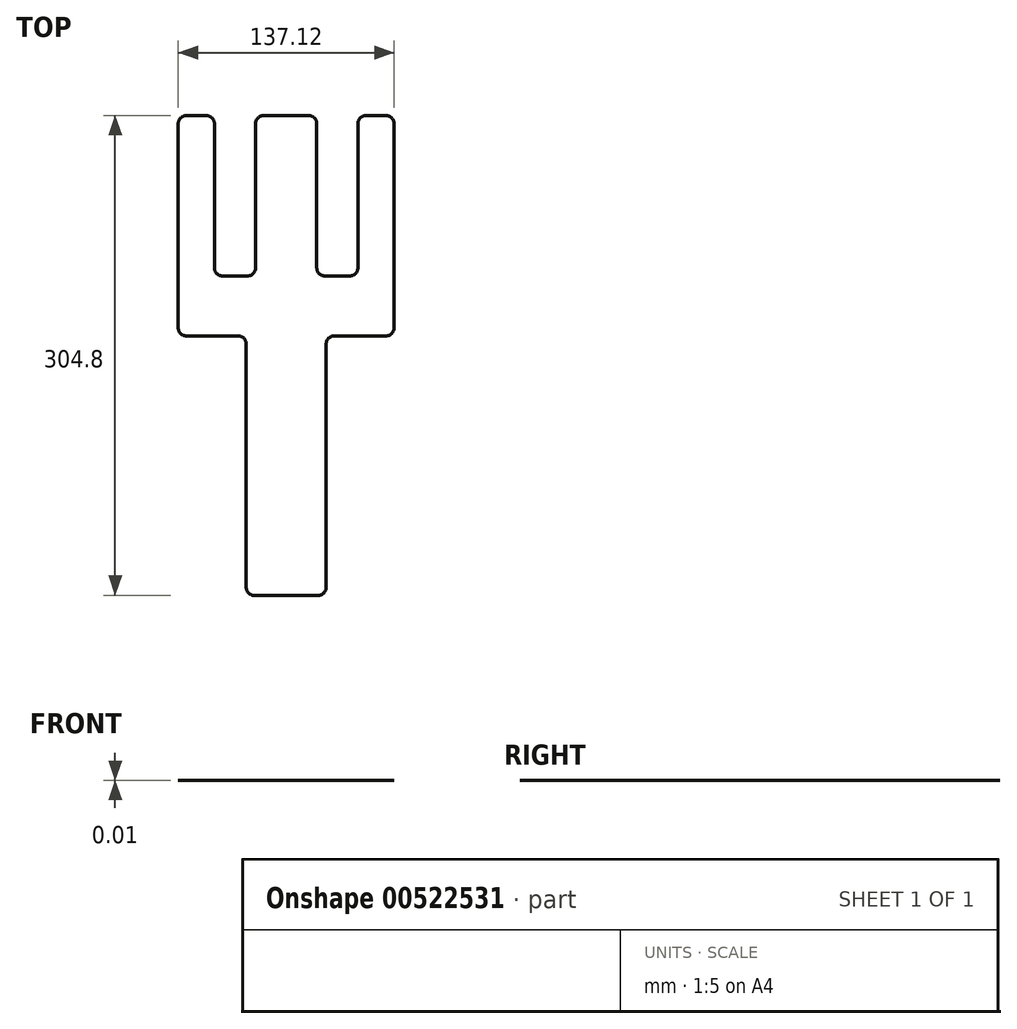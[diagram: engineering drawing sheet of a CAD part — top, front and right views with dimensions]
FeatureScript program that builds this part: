
annotation { "Feature Type Name" : "Feature", "Feature Type Description" : "" }
export const myFeature = defineFeature(function(context is Context, id is Id, definition is map)
    precondition{}
    {
        {
            var Q0;
            Q0=qCreatedBy(makeId("Top.planeOp"),FACE);
            var sketch = newSketch(context, id + "F0", { "sketchPlane" : qUnion([Q0])});
            skLineSegment(sketch, "E0", {"start": v(0, 304.8) * mm, "end": v(-19.44, 304.8) * mm});
            skLineSegment(sketch, "E1", {"start": v(-19.44, 304.8) * mm, "end": v(-19.44, 202.9) * mm});
            skLineSegment(sketch, "E2", {"start": v(-19.44, 202.9) * mm, "end": v(-45.56, 202.9) * mm});
            skLineSegment(sketch, "E3", {"start": v(-45.56, 202.9) * mm, "end": v(-45.56, 304.8) * mm});
            skLineSegment(sketch, "E4", {"start": v(-45.56, 304.8) * mm, "end": v(-68.56, 304.8) * mm});
            skLineSegment(sketch, "E5", {"start": v(-68.56, 304.8) * mm, "end": v(-68.56, 164.8) * mm});
            skLineSegment(sketch, "E6", {"start": v(-68.56, 164.8) * mm, "end": v(-25.4, 164.8) * mm});
            skLineSegment(sketch, "E7", {"start": v(-25.4, 164.8) * mm, "end": v(-25.4, 0) * mm});
            skLineSegment(sketch, "E8", {"start": v(-25.4, 0) * mm, "end": v(0, 0) * mm});
            skLineSegment(sketch, "E9.MirrorCS", {"start": v(25.4, 0) * mm, "end": v(0, 0) * mm});
            skLineSegment(sketch, "E10.MirrorCS", {"start": v(68.56, 164.8) * mm, "end": v(25.4, 164.8) * mm});
            skLineSegment(sketch, "E11.MirrorCS", {"start": v(25.4, 164.8) * mm, "end": v(25.4, 0) * mm});
            skLineSegment(sketch, "E12.MirrorCS", {"start": v(68.56, 304.8) * mm, "end": v(68.56, 164.8) * mm});
            skLineSegment(sketch, "E13.MirrorCS", {"start": v(45.56, 304.8) * mm, "end": v(68.56, 304.8) * mm});
            skLineSegment(sketch, "E14.MirrorCS", {"start": v(45.56, 202.9) * mm, "end": v(45.56, 304.8) * mm});
            skLineSegment(sketch, "E15.MirrorCS", {"start": v(19.44, 202.9) * mm, "end": v(45.56, 202.9) * mm});
            skLineSegment(sketch, "E16.MirrorCS", {"start": v(19.44, 304.8) * mm, "end": v(19.44, 202.9) * mm});
            skLineSegment(sketch, "E17.MirrorCS", {"start": v(0, 304.8) * mm, "end": v(19.44, 304.8) * mm});
            skLineSegment(sketch, "E18", {"start": v(0, 0) * mm, "end": v(0, 304.8) * mm, "construction": true});
            skSolve(sketch);
        }
        {
            var Q0;
            Q0=makeQuery(id+"F0.imprint","IMPRINT",FACE,{"disambiguationData":[TD([[makeQuery(id+"F0.imprint","IMPRINT",EDGE,{"derivedFrom":sQuery(id+"F0.wireOp",EDGE,"E0")}),1.0]])]});
            extrude(context, id + "F1", {"entities" : qUnion([Q0]), "depth" : 3 / 203.2 * mm, "offsetDistance" : 25.4 * mm});
        }
        {
            var Q0;
            Q0=makeQuery(id+"F1.opExtrude","SWEPT_EDGE",EDGE,{"disambiguationData":[OSD([sQuery(id+"F0.wireOp",EDGE,"E12.MirrorCS"),sQuery(id+"F0.wireOp",EDGE,"E13.MirrorCS")])]});
            var Q1;
            Q1=makeQuery(id+"F1.opExtrude","SWEPT_EDGE",EDGE,{"disambiguationData":[OSD([sQuery(id+"F0.wireOp",EDGE,"E13.MirrorCS"),sQuery(id+"F0.wireOp",EDGE,"E14.MirrorCS")])]});
            var Q2;
            Q2=makeQuery(id+"F1.opExtrude","SWEPT_EDGE",EDGE,{"disambiguationData":[OSD([sQuery(id+"F0.wireOp",EDGE,"E16.MirrorCS"),sQuery(id+"F0.wireOp",EDGE,"E17.MirrorCS")])]});
            var Q3;
            Q3=makeQuery(id+"F1.opExtrude","SWEPT_EDGE",EDGE,{"disambiguationData":[OSD([sQuery(id+"F0.wireOp",EDGE,"E0"),sQuery(id+"F0.wireOp",EDGE,"E1")])]});
            var Q4;
            Q4=makeQuery(id+"F1.opExtrude","SWEPT_EDGE",EDGE,{"disambiguationData":[OSD([sQuery(id+"F0.wireOp",EDGE,"E3"),sQuery(id+"F0.wireOp",EDGE,"E4")])]});
            var Q5;
            Q5=makeQuery(id+"F1.opExtrude","SWEPT_EDGE",EDGE,{"disambiguationData":[OSD([sQuery(id+"F0.wireOp",EDGE,"E4"),sQuery(id+"F0.wireOp",EDGE,"E5")])]});
            var Q6;
            Q6=makeQuery(id+"F1.opExtrude","SWEPT_EDGE",EDGE,{"disambiguationData":[OSD([sQuery(id+"F0.wireOp",EDGE,"E10.MirrorCS"),sQuery(id+"F0.wireOp",EDGE,"E12.MirrorCS")])]});
            var Q7;
            Q7=makeQuery(id+"F1.opExtrude","SWEPT_EDGE",EDGE,{"disambiguationData":[OSD([sQuery(id+"F0.wireOp",EDGE,"E6"),sQuery(id+"F0.wireOp",EDGE,"E7")])]});
            var Q8;
            Q8=makeQuery(id+"F1.opExtrude","SWEPT_EDGE",EDGE,{"disambiguationData":[OSD([sQuery(id+"F0.wireOp",EDGE,"E5"),sQuery(id+"F0.wireOp",EDGE,"E6")])]});
            var Q9;
            Q9=makeQuery(id+"F1.opExtrude","SWEPT_EDGE",EDGE,{"disambiguationData":[OSD([sQuery(id+"F0.wireOp",EDGE,"E2"),sQuery(id+"F0.wireOp",EDGE,"E3")])]});
            var Q10;
            Q10=makeQuery(id+"F1.opExtrude","SWEPT_EDGE",EDGE,{"disambiguationData":[OSD([sQuery(id+"F0.wireOp",EDGE,"E15.MirrorCS"),sQuery(id+"F0.wireOp",EDGE,"E16.MirrorCS")])]});
            var Q11;
            Q11=makeQuery(id+"F1.opExtrude","SWEPT_EDGE",EDGE,{"disambiguationData":[OSD([sQuery(id+"F0.wireOp",EDGE,"E1"),sQuery(id+"F0.wireOp",EDGE,"E2")])]});
            var Q12;
            Q12=makeQuery(id+"F1.opExtrude","SWEPT_EDGE",EDGE,{"disambiguationData":[OSD([sQuery(id+"F0.wireOp",EDGE,"E14.MirrorCS"),sQuery(id+"F0.wireOp",EDGE,"E15.MirrorCS")])]});
            var Q13;
            Q13=makeQuery(id+"F1.opExtrude","SWEPT_EDGE",EDGE,{"disambiguationData":[OSD([sQuery(id+"F0.wireOp",EDGE,"E10.MirrorCS"),sQuery(id+"F0.wireOp",EDGE,"E11.MirrorCS")])]});
            var Q14;
            Q14=makeQuery(id+"F1.opExtrude","SWEPT_EDGE",EDGE,{"disambiguationData":[OSD([sQuery(id+"F0.wireOp",EDGE,"E9.MirrorCS"),sQuery(id+"F0.wireOp",EDGE,"E11.MirrorCS")])]});
            var Q15;
            Q15=makeQuery(id+"F1.opExtrude","SWEPT_EDGE",EDGE,{"disambiguationData":[OSD([sQuery(id+"F0.wireOp",EDGE,"E7"),sQuery(id+"F0.wireOp",EDGE,"E8")])]});
            fillet(context, id + "F2", {"entities" : qUnion([Q0, Q1, Q2, Q3, Q4, Q5, Q6, Q7, Q8, Q9, Q10, Q11, Q12, Q13, Q14, Q15]), "radius" : 5.08 * mm, "tangentPropagation" : true, "allowEdgeOverflow" : false});
        }
    });
